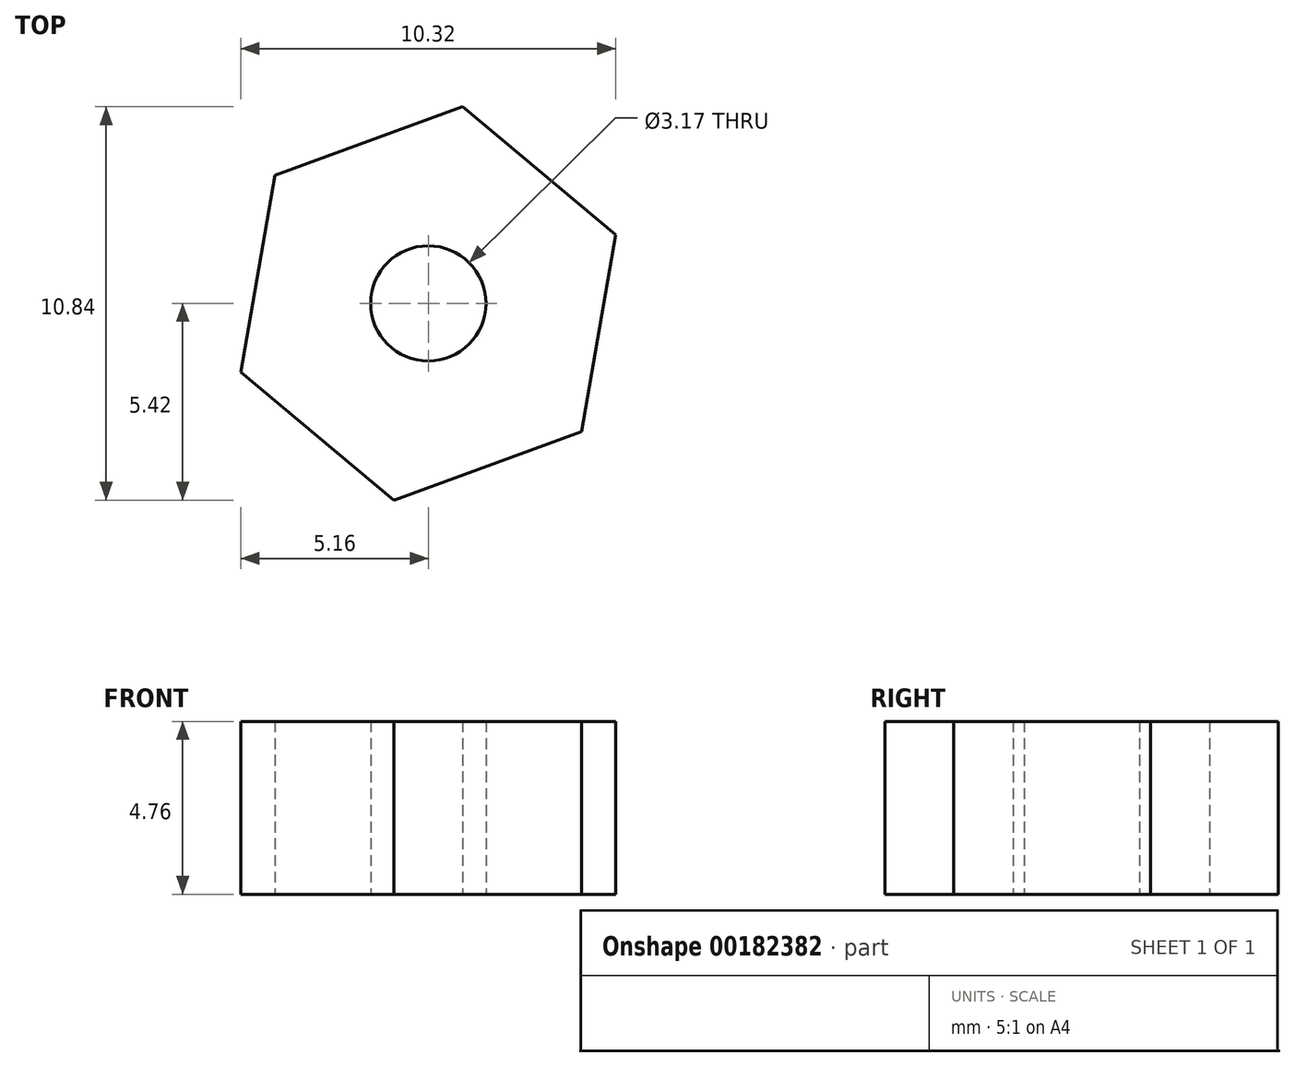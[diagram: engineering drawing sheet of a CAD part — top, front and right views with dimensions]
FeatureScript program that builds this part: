
annotation { "Feature Type Name" : "Feature", "Feature Type Description" : "" }
export const myFeature = defineFeature(function(context is Context, id is Id, definition is map)
    precondition{}
    {
        {
            var Q0;
            Q0=qCreatedBy(makeId("Top.planeOp"),FACE);
            var sketch = newSketch(context, id + "F0", { "sketchPlane" : qUnion([Q0])});
            skCircle(sketch, "E0.cCircle", {"center": v(0, 0) * mm, "radius": 4.76 * mm, "construction": true});
            skLineSegment(sketch, "E0.0", {"start": v(4.22, -3.53) * mm, "end": v(-0.94, -5.42) * mm});
            skLineSegment(sketch, "E0.1", {"start": v(-0.94, -5.42) * mm, "end": v(-5.16, -1.9) * mm});
            skLineSegment(sketch, "E0.2", {"start": v(-5.16, -1.9) * mm, "end": v(-4.22, 3.53) * mm});
            skLineSegment(sketch, "E0.3", {"start": v(-4.22, 3.53) * mm, "end": v(0.94, 5.42) * mm});
            skLineSegment(sketch, "E0.4", {"start": v(0.94, 5.42) * mm, "end": v(5.16, 1.9) * mm});
            skLineSegment(sketch, "E0.5", {"start": v(5.16, 1.9) * mm, "end": v(4.22, -3.53) * mm});
            skPoint(sketch, "E0.0.midPoint", {"position": v(1.64, -4.47) * mm});
            skCircle(sketch, "E1", {"center": v(0, 0) * mm, "radius": 1.59 * mm});
            skSolve(sketch);
        }
        {
            var Q0;
            Q0 = qSketchRegion(id + "F0", true);
            extrude(context, id + "F1", {"entities" : qUnion([Q0]), "depth" : 4.76 * mm});
        }
    });
